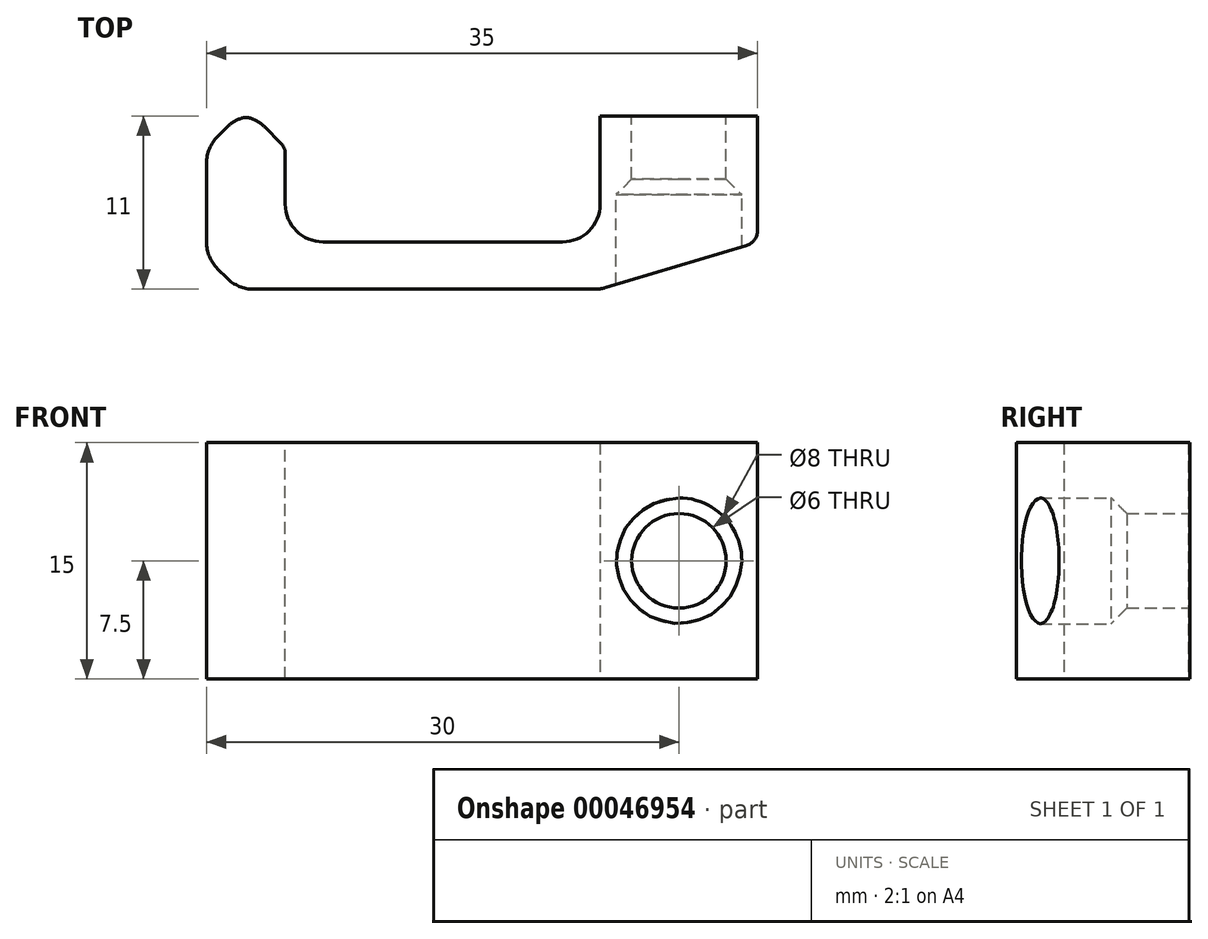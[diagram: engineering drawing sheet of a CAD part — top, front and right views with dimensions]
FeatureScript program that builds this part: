
annotation { "Feature Type Name" : "Feature", "Feature Type Description" : "" }
export const myFeature = defineFeature(function(context is Context, id is Id, definition is map)
    precondition{}
    {
        {
            var Q0;
            Q0=qCreatedBy(makeId("Top.planeOp"),FACE);
            var sketch = newSketch(context, id + "F0", { "sketchPlane" : qUnion([Q0])});
            skLineSegment(sketch, "E0.top", {"start": v(0, -8) * mm, "end": v(20, -8) * mm});
            skLineSegment(sketch, "E0.left", {"start": v(0, 0) * mm, "end": v(0, -8) * mm});
            skLineSegment(sketch, "E0.right", {"start": v(20, 0) * mm, "end": v(20, -8) * mm});
            skLineSegment(sketch, "E1.bottom", {"start": v(20, 0) * mm, "end": v(30, 0) * mm});
            skLineSegment(sketch, "E1.top", {"start": v(20, -8) * mm, "end": v(30, -8) * mm});
            skLineSegment(sketch, "E1.right", {"start": v(30, 0) * mm, "end": v(30, -8) * mm});
            skLineSegment(sketch, "E2.bottom", {"start": v(0, 0) * mm, "end": v(-5, 0) * mm});
            skLineSegment(sketch, "E2.top", {"start": v(20, -11) * mm, "end": v(-5, -11) * mm});
            skLineSegment(sketch, "E2.left", {"start": v(20, 0) * mm, "end": v(20, -11) * mm});
            skLineSegment(sketch, "E2.right", {"start": v(-5, 0) * mm, "end": v(-5, -11) * mm});
            skLineSegment(sketch, "E3", {"start": v(20, -11) * mm, "end": v(30, -8) * mm});
            skSolve(sketch);
        }
        {
            var Q0;
            Q0 = qSketchRegion(id + "F0", true);
            extrude(context, id + "F1", {"entities" : qUnion([Q0]), "depth" : 15 * mm});
        }
        {
            var Q0;
            Q0=makeQuery(id+"F1.opExtrude","SWEPT_FACE",FACE,{"disambiguationData":[OSD([sQuery(id+"F0.wireOp",EDGE,"E1.bottom")])]});
            var sketch = newSketch(context, id + "F2", { "sketchPlane" : qUnion([Q0])});
            skLineSegment(sketch, "E4", {"start": v(-30, 15) * mm, "end": v(-20, 0) * mm, "construction": true});
            skCircle(sketch, "E5", {"center": v(-25, 7.5) * mm, "radius": 4 * mm});
            skCircle(sketch, "E6", {"center": v(-25, 7.5) * mm, "radius": 3 * mm});
            skSolve(sketch);
        }
        {
            var Q0;
            Q0 = qSketchRegion(id + "F2", true);
            var Q1;
            Q1=makeQuery(id+"F2.imprint","IMPRINT",FACE,{"disambiguationData":[TD([[makeQuery(id+"F2.imprint","IMPRINT",EDGE,{"derivedFrom":sQuery(id+"F2.wireOp",EDGE,"E6")}),1.0]])]});
            extrude(context, id + "F3", {"entities" : qUnion([Q0, Q1]), "operationType" : NewBodyOperationType.REMOVE, "oppositeDirection" : true, "depth" : 25 * mm});
        }
        {
            var Q0;
            Q0=makeQuery(id+"F2.imprint","IMPRINT",FACE,{"disambiguationData":[TD([[makeQuery(id+"F2.imprint","IMPRINT",EDGE,{"derivedFrom":sQuery(id+"F2.wireOp",EDGE,"E5")}),1.0]])]});
            extrude(context, id + "F4", {"entities" : qUnion([Q0]), "operationType" : NewBodyOperationType.ADD, "oppositeDirection" : true, "depth" : 5 * mm});
        }
        {
            var Q0;
            Q0=makeQuery(id+"F4.opExtrude","CAP_EDGE",EDGE,{"disambiguationData":[OSD([sQuery(id+"F2.wireOp",EDGE,"E6")])],"isStart":false});
            chamfer(context, id + "F5", {"entities" : qUnion([Q0]), "width" : 1 * mm, "tangentPropagation" : true});
        }
        {
            var Q0;
            Q0=makeQuery(id+"F1.opExtrude","SWEPT_EDGE",EDGE,{"disambiguationData":[OSD([sQuery(id+"F0.wireOp",EDGE,"E2.bottom"),sQuery(id+"F0.wireOp",EDGE,"E2.right")])]});
            var Q1;
            Q1=makeQuery(id+"F1.opExtrude","SWEPT_EDGE",EDGE,{"disambiguationData":[OSD([sQuery(id+"F0.wireOp",EDGE,"E0.left"),sQuery(id+"F0.wireOp",EDGE,"E2.bottom")])]});
            var Q2;
            Q2=makeQuery(id+"F1.opExtrude","SWEPT_EDGE",EDGE,{"disambiguationData":[OSD([sQuery(id+"F0.wireOp",EDGE,"E2.top"),sQuery(id+"F0.wireOp",EDGE,"E2.right")])]});
            chamfer(context, id + "F6", {"entities" : qUnion([Q0, Q1, Q2]), "width" : 2 * mm, "tangentPropagation" : true});
        }
        {
            var Q0;
            {var subQ0=sQuery(id+"F0.wireOp",EDGE,"E2.bottom");Q0=makeQuery(id+"F6.opChamfer","BLEND_EDGE",EDGE,{"blendedFrom":[makeQuery(id+"F1.opExtrude","SWEPT_EDGE",EDGE,{"disambiguationData":[OSD([sQuery(id+"F0.wireOp",EDGE,"E0.left"),subQ0])]}),makeQuery(id+"F1.opExtrude","SWEPT_FACE",FACE,{"disambiguationData":[OSD([subQ0])]})],"blendedInto":[makeQuery(id+"F1.opExtrude","SWEPT_FACE",FACE,{"disambiguationData":[OSD([subQ0])]})]});}
            var Q1;
            {var subQ0=sQuery(id+"F0.wireOp",EDGE,"E2.bottom");Q1=makeQuery(id+"F6.opChamfer","BLEND_EDGE",EDGE,{"blendedFrom":[makeQuery(id+"F1.opExtrude","SWEPT_EDGE",EDGE,{"disambiguationData":[OSD([subQ0,sQuery(id+"F0.wireOp",EDGE,"E2.right")])]}),makeQuery(id+"F1.opExtrude","SWEPT_FACE",FACE,{"disambiguationData":[OSD([subQ0])]})],"blendedInto":[makeQuery(id+"F1.opExtrude","SWEPT_FACE",FACE,{"disambiguationData":[OSD([subQ0])]})]});}
            var Q2;
            Q2=makeQuery(id+"F1.opExtrude","SWEPT_EDGE",EDGE,{"disambiguationData":[OSD([sQuery(id+"F0.wireOp",EDGE,"E0.top"),sQuery(id+"F0.wireOp",EDGE,"E0.left")])]});
            var Q3;
            Q3=makeQuery(id+"F1.opExtrude","SWEPT_EDGE",EDGE,{"disambiguationData":[OSD([sQuery(id+"F0.wireOp",EDGE,"E0.top"),sQuery(id+"F0.wireOp",EDGE,"E1.top"),sQuery(id+"F0.wireOp",EDGE,"E2.left")])]});
            var Q4;
            {var subQ0=sQuery(id+"F0.wireOp",EDGE,"E2.right");Q4=makeQuery(id+"F6.opChamfer","BLEND_EDGE",EDGE,{"blendedFrom":[makeQuery(id+"F1.opExtrude","SWEPT_EDGE",EDGE,{"disambiguationData":[OSD([sQuery(id+"F0.wireOp",EDGE,"E2.bottom"),subQ0])]}),makeQuery(id+"F1.opExtrude","SWEPT_FACE",FACE,{"disambiguationData":[OSD([subQ0])]})],"blendedInto":[makeQuery(id+"F1.opExtrude","SWEPT_FACE",FACE,{"disambiguationData":[OSD([subQ0])]})]});}
            var Q5;
            {var subQ0=sQuery(id+"F0.wireOp",EDGE,"E2.right");Q5=makeQuery(id+"F6.opChamfer","BLEND_EDGE",EDGE,{"blendedFrom":[makeQuery(id+"F1.opExtrude","SWEPT_EDGE",EDGE,{"disambiguationData":[OSD([sQuery(id+"F0.wireOp",EDGE,"E2.top"),subQ0])]}),makeQuery(id+"F1.opExtrude","SWEPT_FACE",FACE,{"disambiguationData":[OSD([subQ0])]})],"blendedInto":[makeQuery(id+"F1.opExtrude","SWEPT_FACE",FACE,{"disambiguationData":[OSD([subQ0])]})]});}
            var Q6;
            {var subQ0=sQuery(id+"F0.wireOp",EDGE,"E2.top");Q6=makeQuery(id+"F6.opChamfer","BLEND_EDGE",EDGE,{"blendedFrom":[makeQuery(id+"F1.opExtrude","SWEPT_EDGE",EDGE,{"disambiguationData":[OSD([subQ0,sQuery(id+"F0.wireOp",EDGE,"E2.right")])]}),makeQuery(id+"F1.opExtrude","SWEPT_FACE",FACE,{"disambiguationData":[OSD([subQ0])]})],"blendedInto":[makeQuery(id+"F1.opExtrude","SWEPT_FACE",FACE,{"disambiguationData":[OSD([subQ0])]})]});}
            var Q7;
            Q7=makeQuery(id+"F1.opExtrude","SWEPT_EDGE",EDGE,{"disambiguationData":[OSD([sQuery(id+"F0.wireOp",EDGE,"E2.top"),sQuery(id+"F0.wireOp",EDGE,"E2.left"),sQuery(id+"F0.wireOp",EDGE,"E3")])]});
            fillet(context, id + "F7", {"entities" : qUnion([Q0, Q1, Q2, Q3, Q4, Q5, Q6, Q7]), "radius" : 2.4 * mm, "tangentPropagation" : true, "allowEdgeOverflow" : false});
        }
        {
            var Q0;
            {var subQ0=sQuery(id+"F0.wireOp",EDGE,"E2.bottom");var subQ1=makeQuery(id+"F1.opExtrude","SWEPT_FACE",FACE,{"disambiguationData":[OSD([subQ0])]});Q0=makeQuery(id+"F7.opFillet","BLEND_EDGE",EDGE,{"blendedFrom":[makeQuery(id+"F6.opChamfer","BLEND_EDGE",EDGE,{"blendedFrom":[makeQuery(id+"F1.opExtrude","SWEPT_EDGE",EDGE,{"disambiguationData":[OSD([sQuery(id+"F0.wireOp",EDGE,"E0.left"),subQ0])]}),subQ1],"blendedInto":[subQ1]}),makeQuery(id+"F6.opChamfer","BLEND_EDGE",EDGE,{"blendedFrom":[makeQuery(id+"F1.opExtrude","SWEPT_EDGE",EDGE,{"disambiguationData":[OSD([subQ0,sQuery(id+"F0.wireOp",EDGE,"E2.right")])]}),subQ1],"blendedInto":[subQ1]})],"blendedInto":[]});}
            var Q1;
            {var subQ0=sQuery(id+"F0.wireOp",EDGE,"E0.left");Q1=makeQuery(id+"F6.opChamfer","BLEND_EDGE",EDGE,{"blendedFrom":[makeQuery(id+"F1.opExtrude","SWEPT_EDGE",EDGE,{"disambiguationData":[OSD([subQ0,sQuery(id+"F0.wireOp",EDGE,"E2.bottom")])]}),makeQuery(id+"F1.opExtrude","SWEPT_FACE",FACE,{"disambiguationData":[OSD([subQ0])]})],"blendedInto":[makeQuery(id+"F1.opExtrude","SWEPT_FACE",FACE,{"disambiguationData":[OSD([subQ0])]})]});}
            var Q2;
            Q2=makeQuery(id+"F1.opExtrude","SWEPT_EDGE",EDGE,{"disambiguationData":[OSD([sQuery(id+"F0.wireOp",EDGE,"E1.top"),sQuery(id+"F0.wireOp",EDGE,"E1.right"),sQuery(id+"F0.wireOp",EDGE,"E3")])]});
            fillet(context, id + "F8", {"entities" : qUnion([Q0, Q1, Q2]), "radius" : 1 * mm, "tangentPropagation" : true, "allowEdgeOverflow" : false});
        }
    });
